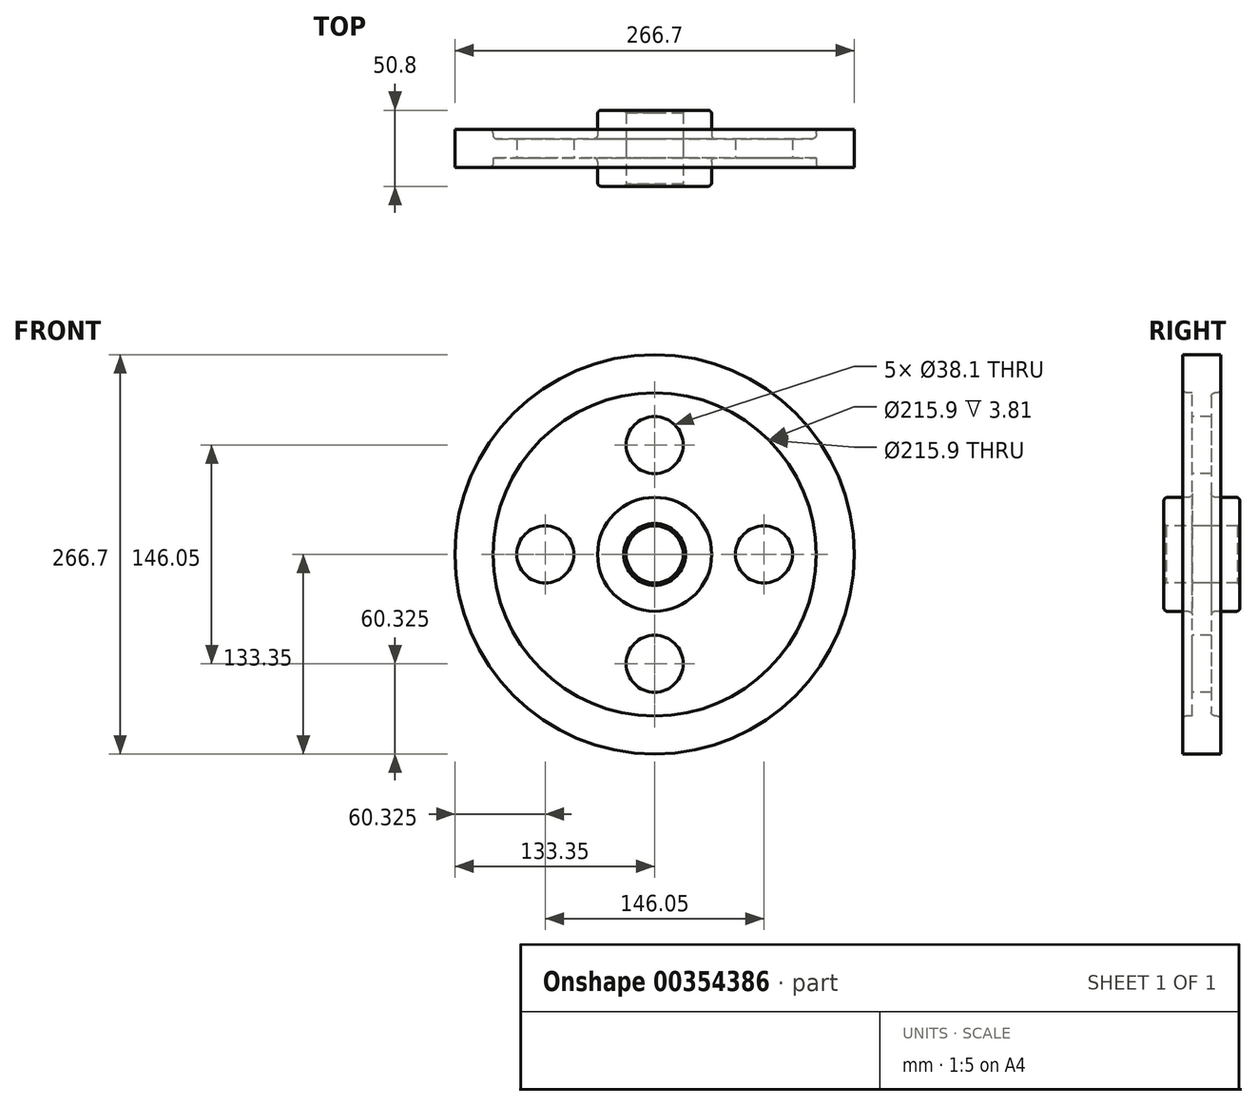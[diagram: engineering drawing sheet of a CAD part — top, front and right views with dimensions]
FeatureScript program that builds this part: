
annotation { "Feature Type Name" : "Feature", "Feature Type Description" : "" }
export const myFeature = defineFeature(function(context is Context, id is Id, definition is map)
    precondition{}
    {
        {
            var Q0;
            Q0=qCreatedBy(makeId("Right.planeOp"),FACE);
            var sketch = newSketch(context, id + "F0", { "sketchPlane" : qUnion([Q0])});
            skLineSegment(sketch, "E0", {"start": v(0, 0) * mm, "end": v(25.4, 0) * mm});
            skLineSegment(sketch, "E1.0", {"start": v(0, 19.05) * mm, "end": v(25.4, 19.05) * mm});
            skLineSegment(sketch, "E2.0", {"start": v(6.35, 38.1) * mm, "end": v(25.4, 38.1) * mm});
            skLineSegment(sketch, "E3.0", {"start": v(6.35, 107.95) * mm, "end": v(12.7, 107.95) * mm});
            skLineSegment(sketch, "E4.0", {"start": v(0, 133.35) * mm, "end": v(12.7, 133.35) * mm});
            skLineSegment(sketch, "E5", {"start": v(0, 133.35) * mm, "end": v(0, 0) * mm});
            skLineSegment(sketch, "E6.MirrorCS", {"start": v(6.35, 107.95) * mm, "end": v(6.35, 38.1) * mm});
            skLineSegment(sketch, "E7.MirrorCS", {"start": v(12.7, 133.35) * mm, "end": v(12.7, 107.95) * mm});
            skLineSegment(sketch, "E8.MirrorCS", {"start": v(25.4, 38.1) * mm, "end": v(25.4, 19.05) * mm});
            skPoint(sketch, "E9.0.end.orphan", {"position": v(-25.4, 0) * mm});
            skPoint(sketch, "E9.0.start.orphan", {"position": v(-25.4, 133.35) * mm});
            skPoint(sketch, "E10.0.end.orphan", {"position": v(-12.7, 0) * mm});
            skPoint(sketch, "E10.0.start.orphan", {"position": v(-12.7, 133.35) * mm});
            skPoint(sketch, "E11.0.end.orphan", {"position": v(-6.35, 0) * mm});
            skPoint(sketch, "E11.0.start.orphan", {"position": v(-6.35, 133.35) * mm});
            skPoint(sketch, "E12.orphan", {"position": v(25.4, 133.35) * mm});
            skPoint(sketch, "E13.orphan", {"position": v(12.7, 0) * mm});
            skPoint(sketch, "E14.orphan", {"position": v(6.35, 0) * mm});
            skPoint(sketch, "E15.orphan", {"position": v(6.35, 133.35) * mm});
            skLineSegment(sketch, "E16", {"start": v(0, 133.35) * mm, "end": v(6.35, 133.35) * mm});
            skLineSegment(sketch, "E17.MirrorCS", {"start": v(-12.7, 133.35) * mm, "end": v(-12.7, 107.95) * mm});
            skLineSegment(sketch, "E18.MirrorCS", {"start": v(-6.35, 107.95) * mm, "end": v(-6.35, 38.1) * mm});
            skLineSegment(sketch, "E19.MirrorCS", {"start": v(-6.35, 107.95) * mm, "end": v(-12.7, 107.95) * mm});
            skLineSegment(sketch, "E20.MirrorCS", {"start": v(-6.35, 38.1) * mm, "end": v(-25.4, 38.1) * mm});
            skLineSegment(sketch, "E21.MirrorCS", {"start": v(0, 19.05) * mm, "end": v(-25.4, 19.05) * mm});
            skLineSegment(sketch, "E22.MirrorCS", {"start": v(-25.4, 38.1) * mm, "end": v(-25.4, 19.05) * mm});
            skLineSegment(sketch, "E23", {"start": v(-12.7, 133.35) * mm, "end": v(0, 133.35) * mm});
            skLineSegment(sketch, "E24", {"start": v(-2.7, 133.18) * mm, "end": v(-12.7, 133.35) * mm});
            skLineSegment(sketch, "E25", {"start": v(-12.7, 133.35) * mm, "end": v(12.7, 133.35) * mm});
            skSolve(sketch);
        }
        {
            var Q0;
            {var subQ0=sQuery(id+"F0.wireOp",EDGE,"E17.MirrorCS");Q0=makeQuery(id+"F0.imprint","IMPRINT",FACE,{"disambiguationData":[TD([[makeQuery(id+"F0.imprint","IMPRINT",EDGE,{"derivedFrom":subQ0}),1.0]])]});}
            var Q1;
            {var subQ1=sQuery(id+"F0.wireOp",EDGE,"E1.0");Q1=makeQuery(id+"F0.imprint","IMPRINT",FACE,{"disambiguationData":[TD([[makeQuery(id+"F0.imprint","IMPRINT",EDGE,{"derivedFrom":subQ1}),1.0]])]});}
            var Q2;
            Q2=sQuery(id+"F0.wireOp",EDGE,"E0");
            revolve(context, id + "F1", {"entities" : qUnion([Q0, Q1]), "axis" : qUnion([Q2]), "revolveType" : RevolveType.FULL});
        }
        {
            var Q0;
            Q0=makeQuery(id+"F1.opRevolve","SWEPT_FACE",FACE,{"disambiguationData":[OSD([sQuery(id+"F0.wireOp",EDGE,"E18.MirrorCS")])]});
            var sketch = newSketch(context, id + "F2", { "sketchPlane" : qUnion([Q0])});
            skLineSegment(sketch, "E26", {"start": v(0, 0) * mm, "end": v(0, 73.03) * mm});
            skCircle(sketch, "E27", {"center": v(0, 73.03) * mm, "radius": 19.05 * mm});
            skCircle(sketch, "E28.1.0", {"center": v(-73.03, 0) * mm, "radius": 19.05 * mm});
            skCircle(sketch, "E28.2.0", {"center": v(0, -73.03) * mm, "radius": 19.05 * mm});
            skCircle(sketch, "E28.3.0", {"center": v(73.03, 0) * mm, "radius": 19.05 * mm});
            skPoint(sketch, "E28.center", {"position": v(0, 0) * mm});
            skSolve(sketch);
        }
        {
            var Q0;
            Q0=makeQuery(id+"F2.imprint","IMPRINT",FACE,{"disambiguationData":[TD([[makeQuery(id+"F2.imprint","IMPRINT",EDGE,{"derivedFrom":sQuery(id+"F2.wireOp",EDGE,"E28.1.0")}),1.0]])]});
            var Q1;
            Q1=makeQuery(id+"F2.imprint","IMPRINT",FACE,{"disambiguationData":[TD([[makeQuery(id+"F2.imprint","IMPRINT",EDGE,{"derivedFrom":sQuery(id+"F2.wireOp",EDGE,"E28.2.0")}),1.0]])]});
            var Q2;
            Q2=makeQuery(id+"F2.imprint","IMPRINT",FACE,{"disambiguationData":[TD([[makeQuery(id+"F2.imprint","IMPRINT",EDGE,{"derivedFrom":sQuery(id+"F2.wireOp",EDGE,"E28.3.0")}),1.0]])]});
            var Q3;
            Q3=makeQuery(id+"F2.imprint","IMPRINT",FACE,{"disambiguationData":[TD([[makeQuery(id+"F2.imprint","IMPRINT",EDGE,{"derivedFrom":sQuery(id+"F2.wireOp",EDGE,"E27")}),1.0]])]});
            extrude(context, id + "F3", {"entities" : qUnion([Q0, Q1, Q2, Q3]), "operationType" : NewBodyOperationType.REMOVE, "oppositeDirection" : true, "depth" : 25.4 * mm});
        }
        {
            var Q0;
            Q0=makeQuery(id+"F1.opRevolve","SWEPT_EDGE",EDGE,{"disambiguationData":[OSD([sQuery(id+"F0.wireOp",EDGE,"E17.MirrorCS"),sQuery(id+"F0.wireOp",EDGE,"E19.MirrorCS")])]});
            var Q1;
            Q1=makeQuery(id+"F1.opRevolve","SWEPT_EDGE",EDGE,{"disambiguationData":[OSD([sQuery(id+"F0.wireOp",EDGE,"E20.MirrorCS"),sQuery(id+"F0.wireOp",EDGE,"E22.MirrorCS")])]});
            var Q2;
            Q2=makeQuery(id+"F1.opRevolve","SWEPT_EDGE",EDGE,{"disambiguationData":[OSD([sQuery(id+"F0.wireOp",EDGE,"E18.MirrorCS"),sQuery(id+"F0.wireOp",EDGE,"E20.MirrorCS")])]});
            fillet(context, id + "F4", {"entities" : qUnion([Q0, Q1, Q2]), "radius" : 2.54 * mm, "tangentPropagation" : true, "allowEdgeOverflow" : false});
        }
        {
            var Q0;
            Q0=makeQuery(id+"F1.opRevolve","SWEPT_EDGE",EDGE,{"disambiguationData":[OSD([sQuery(id+"F0.wireOp",EDGE,"E3.0"),sQuery(id+"F0.wireOp",EDGE,"E6.MirrorCS")])]});
            var Q1;
            Q1=makeQuery(id+"F1.opRevolve","SWEPT_EDGE",EDGE,{"disambiguationData":[OSD([sQuery(id+"F0.wireOp",EDGE,"E3.0"),sQuery(id+"F0.wireOp",EDGE,"E7.MirrorCS")])]});
            var Q2;
            Q2=makeQuery(id+"F1.opRevolve","SWEPT_EDGE",EDGE,{"disambiguationData":[OSD([sQuery(id+"F0.wireOp",EDGE,"E2.0"),sQuery(id+"F0.wireOp",EDGE,"E6.MirrorCS")])]});
            fillet(context, id + "F5", {"entities" : qUnion([Q0, Q1, Q2]), "radius" : 2.54 * mm, "tangentPropagation" : true, "allowEdgeOverflow" : false});
        }
        {
            var Q0;
            Q0=makeQuery(id+"F1.opRevolve","SWEPT_EDGE",EDGE,{"disambiguationData":[OSD([sQuery(id+"F0.wireOp",EDGE,"E2.0"),sQuery(id+"F0.wireOp",EDGE,"E8.MirrorCS")])]});
            fillet(context, id + "F6", {"entities" : qUnion([Q0]), "radius" : 2.54 * mm, "tangentPropagation" : true, "allowEdgeOverflow" : false});
        }
        {
            var Q0;
            Q0=makeQuery(id+"F1.opRevolve","SWEPT_EDGE",EDGE,{"disambiguationData":[OSD([sQuery(id+"F0.wireOp",EDGE,"E1.0"),sQuery(id+"F0.wireOp",EDGE,"E8.MirrorCS")])]});
            var Q1;
            Q1=makeQuery(id+"F1.opRevolve","SWEPT_EDGE",EDGE,{"disambiguationData":[OSD([sQuery(id+"F0.wireOp",EDGE,"E21.MirrorCS"),sQuery(id+"F0.wireOp",EDGE,"E22.MirrorCS")])]});
            chamfer(context, id + "F7", {"entities" : qUnion([Q0, Q1]), "width" : 1.59 * mm, "tangentPropagation" : true});
        }
    });
